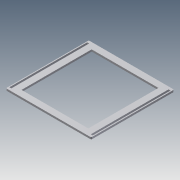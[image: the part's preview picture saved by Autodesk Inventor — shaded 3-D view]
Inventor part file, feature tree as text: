
AUTODESK INVENTOR PART (.ipt)
format: ipt  version: 2014 (Build 180170000, 170)  size: 113,152 bytes
history: native  units: mm
features: extrude x3, sketch x3, mirror x1, fillet x1
ambient origin geometry x8: Origin, YZ Plane, XZ Plane, XY Plane, X Axis, Y Axis, Z Axis, Center Point
bodies: Solid1 (feature_tree)
feature tree (8):
  extrude  "Extrusion1"  Depth=260.38625mm
  extrude  "Extrusion2"  Depth=2.875mm
  mirror  "Mirror1"
  fillet  "Fillet1"  Radius=6.25mm
  extrude  "Extrusion3"  Depth=8.0mm TaperAngle=0.0deg
  sketch  "Sketch1"  dims[d0=268.0mm d1=260.38625mm]
  sketch  "Sketch2"  dims[d2=6.0mm d3=0.0mm d5=2.875mm d6=6.25mm]
  sketch  "Sketch3"  dims[d7=8.0mm d9=4.0mm d10=0.0mm d11=3.0mm d12=20.0mm d13=20.0mm d14=4.0mm d15=0.0mm d101=8.0mm]
